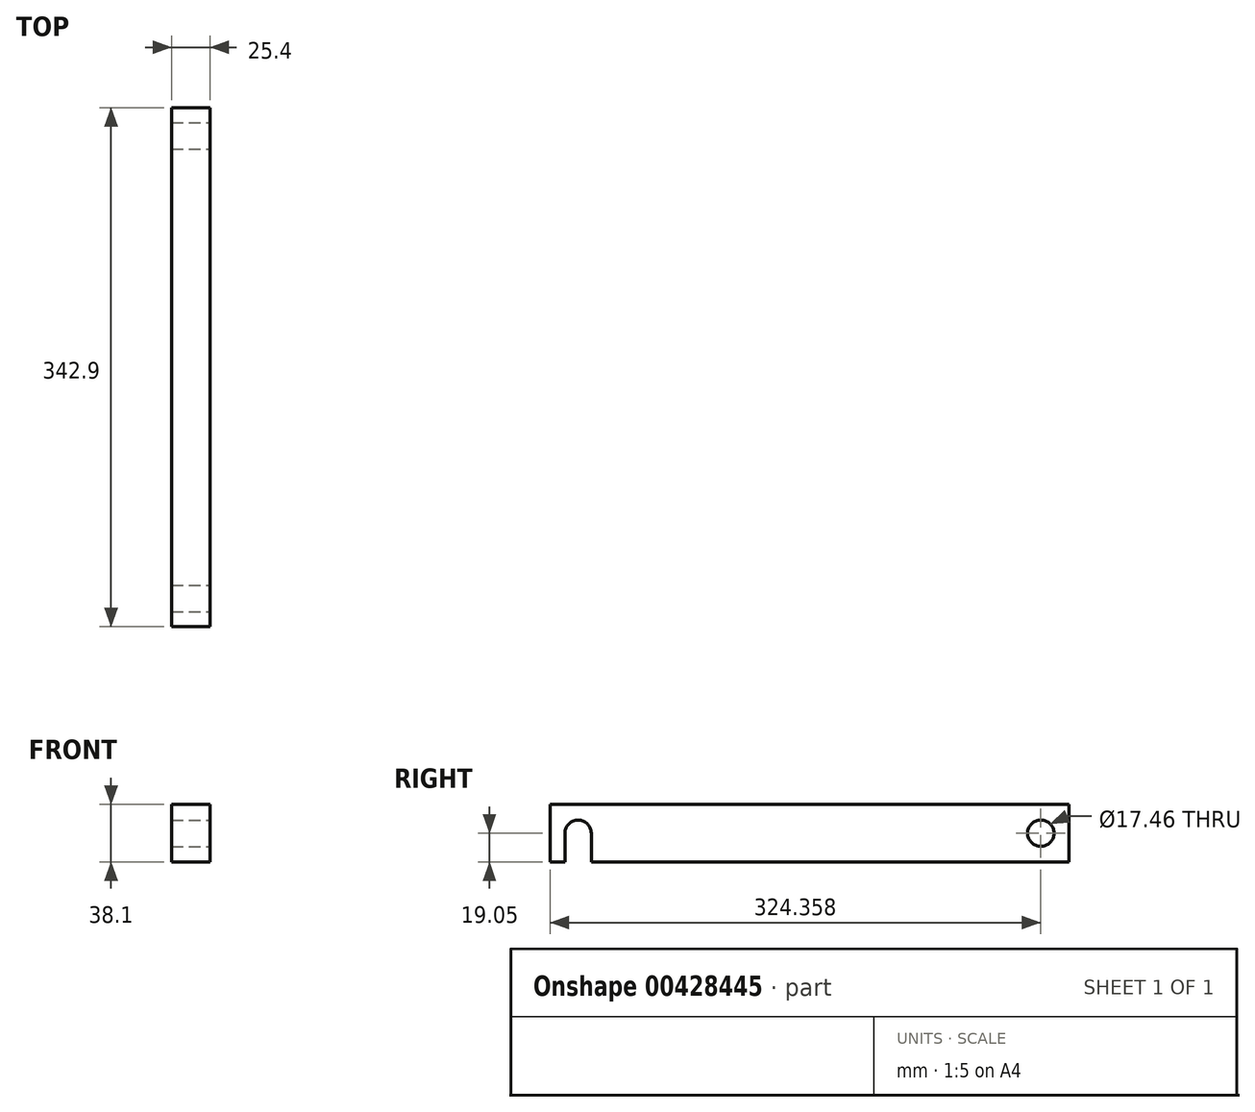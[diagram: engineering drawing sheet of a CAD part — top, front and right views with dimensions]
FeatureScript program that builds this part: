
annotation { "Feature Type Name" : "Feature", "Feature Type Description" : "" }
export const myFeature = defineFeature(function(context is Context, id is Id, definition is map)
    precondition{}
    {
        {
            var Q0;
            Q0=qCreatedBy(makeId("Front.planeOp"),FACE);
            var sketch = newSketch(context, id + "F0", { "sketchPlane" : qUnion([Q0])});
            skLineSegment(sketch, "E0.bottom", {"start": v(12.7, -19.05) * mm, "end": v(-12.7, -19.05) * mm});
            skLineSegment(sketch, "E0.top", {"start": v(12.7, 19.05) * mm, "end": v(-12.7, 19.05) * mm});
            skLineSegment(sketch, "E0.left", {"start": v(12.7, -19.05) * mm, "end": v(12.7, 19.05) * mm});
            skLineSegment(sketch, "E0.right", {"start": v(-12.7, -19.05) * mm, "end": v(-12.7, 19.05) * mm});
            skPoint(sketch, "E0.middle", {"position": v(0, 0) * mm});
            skSolve(sketch);
        }
        {
            var Q0;
            Q0=makeQuery(id+"F0.imprint","IMPRINT",FACE,{"disambiguationData":[TD([[makeQuery(id+"F0.imprint","IMPRINT",EDGE,{"derivedFrom":sQuery(id+"F0.wireOp",EDGE,"E0.bottom")}),-1.0]])]});
            extrude(context, id + "F1", {"entities" : qUnion([Q0]), "depth" : 171.45 * mm, "hasSecondDirection" : true, "secondDirectionOppositeDirection" : true, "secondDirectionDepth" : 171.45 * mm});
        }
        {
            var Q0;
            Q0=makeQuery(id+"F1.opExtrude","SWEPT_FACE",FACE,{"disambiguationData":[OSD([sQuery(id+"F0.wireOp",EDGE,"E0.left")])]});
            var sketch = newSketch(context, id + "F2", { "sketchPlane" : qUnion([Q0])});
            skPoint(sketch, "E1", {"position": v(152.9, 0) * mm});
            skSolve(sketch);
        }
        {
            var Q0;
            Q0=sQuery(id+"F2.wireOp",VERTEX,"E1");
            var Q1;
            Q1=makeQuery(id+"F1.opExtrude","SWEPT_BODY",BODY,{"disambiguationData":[OSD([sQuery(id+"F0.wireOp",EDGE,"E0.bottom"),sQuery(id+"F0.wireOp",EDGE,"E0.top"),sQuery(id+"F0.wireOp",EDGE,"E0.left"),sQuery(id+"F0.wireOp",EDGE,"E0.right")])]});
            hole(context, id + "F3", {"style" : HoleStyle.SIMPLE, "endStyle" : HoleEndStyle.THROUGH, "holeDiameter" : 17.46 * mm, "isTappedThrough" : true, "tappedDepth" : 12.7 * mm, "tapClearance" : 3, "locations" : qUnion([Q0]), "scope" : qUnion([Q1])});
        }
        {
            var Q0;
            Q0=makeQuery(id+"F1.opExtrude","SWEPT_FACE",FACE,{"disambiguationData":[OSD([sQuery(id+"F0.wireOp",EDGE,"E0.left")])]});
            var sketch = newSketch(context, id + "F4", { "sketchPlane" : qUnion([Q0])});
            skArc(sketch, "E2", {"start": v(-144.18, 0) * mm, "mid": v(-152.9, 8.73) * mm, "end": v(-161.64, 0) * mm});
            skLineSegment(sketch, "E3", {"start": v(-144.18, 0) * mm, "end": v(-144.18, -19.05) * mm});
            skLineSegment(sketch, "E4", {"start": v(-161.64, 0) * mm, "end": v(-161.64, -19.24) * mm});
            skLineSegment(sketch, "E5", {"start": v(-161.64, -19.05) * mm, "end": v(-144.18, -19.05) * mm});
            skSolve(sketch);
        }
        {
            var Q0;
            Q0 = qSketchRegion(id + "F4", true);
            extrude(context, id + "F5", {"entities" : qUnion([Q0]), "operationType" : NewBodyOperationType.REMOVE, "oppositeDirection" : true, "depth" : 25.4 * mm});
        }
    });
